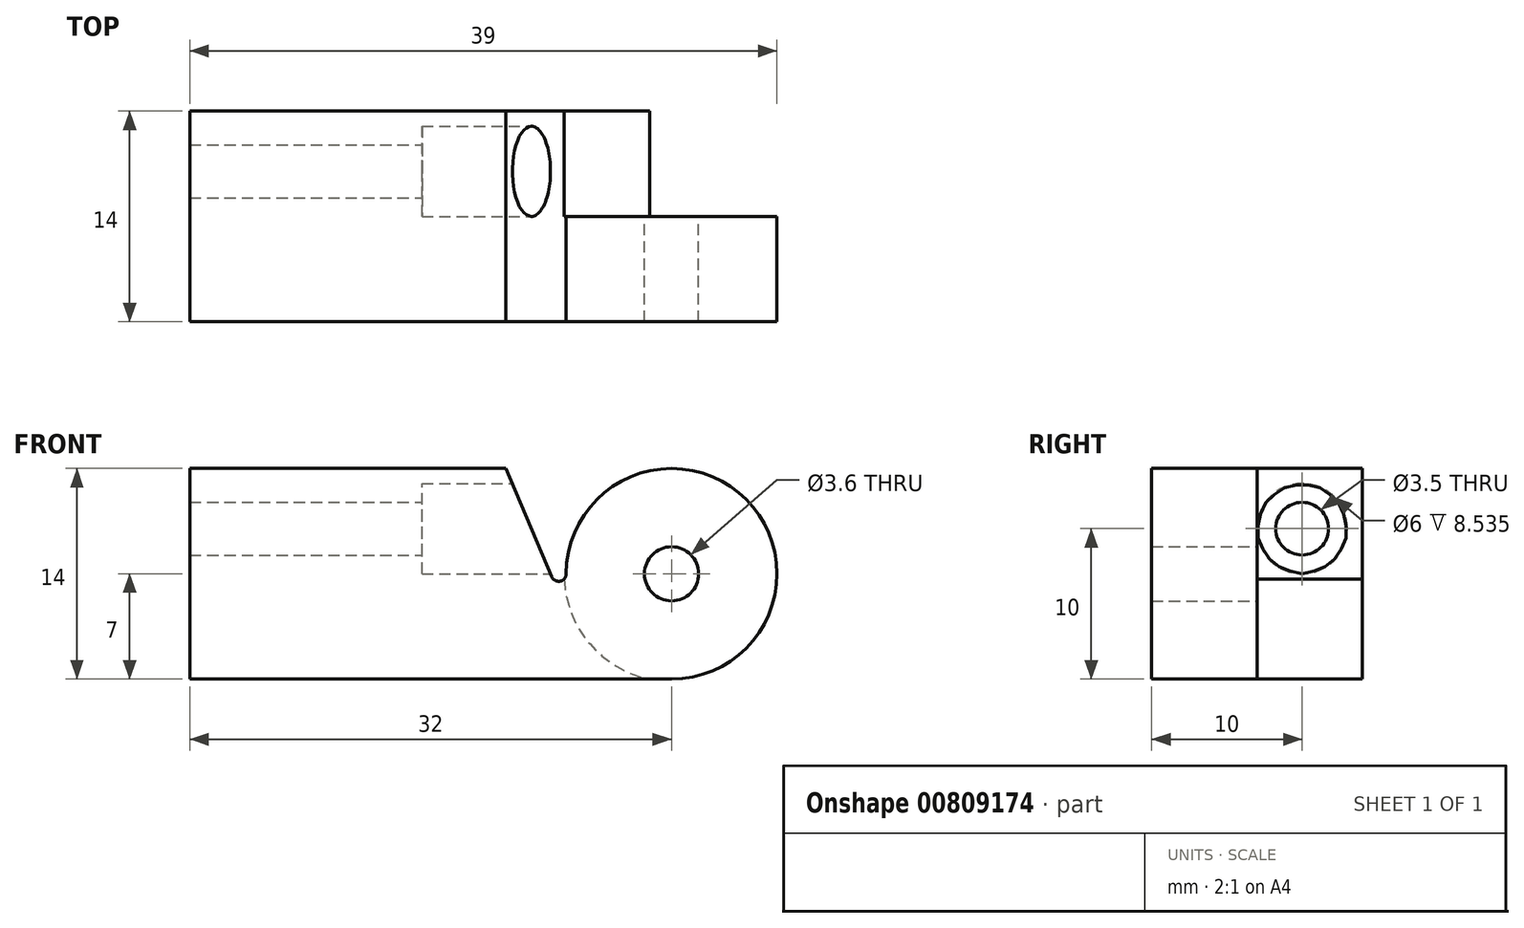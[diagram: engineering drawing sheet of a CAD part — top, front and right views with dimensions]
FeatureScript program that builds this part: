
annotation { "Feature Type Name" : "Feature", "Feature Type Description" : "" }
export const myFeature = defineFeature(function(context is Context, id is Id, definition is map)
    precondition{}
    {
        {
            var Q0;
            Q0=qCreatedBy(makeId("Front.planeOp"),FACE);
            var sketch = newSketch(context, id + "F0", { "sketchPlane" : qUnion([Q0])});
            skLineSegment(sketch, "E0", {"start": v(0, -1.46) * mm, "end": v(0, -7) * mm});
            skLineSegment(sketch, "E1", {"start": v(0, -7) * mm, "end": v(-25, -7) * mm});
            skLineSegment(sketch, "E2", {"start": v(-25, -7) * mm, "end": v(-25, 7) * mm});
            skPoint(sketch, "E3", {"position": v(-1, 0) * mm});
            skArc(sketch, "E4", {"start": v(-1, 0) * mm, "mid": v(-0.5, -0.5) * mm, "end": v(0, 0) * mm});
            skLineSegment(sketch, "E5", {"start": v(-25, 7) * mm, "end": v(-4, 7) * mm});
            skLineSegment(sketch, "E6", {"start": v(-4, 7) * mm, "end": v(-0.96, -0.2) * mm});
            skPoint(sketch, "E7", {"position": v(7, 0) * mm});
            skPoint(sketch, "E8", {"position": v(0, 0) * mm});
            skCircle(sketch, "E9", {"center": v(7, 0) * mm, "radius": 7 * mm});
            skLineSegment(sketch, "E10", {"start": v(0, -7) * mm, "end": v(7, -7) * mm});
            skArc(sketch, "E11", {"start": v(-0.14, -0.35) * mm, "mid": v(1.56, -4.65) * mm, "end": v(5.54, -7) * mm});
            skLineSegment(sketch, "E12", {"start": v(0, 0) * mm, "end": v(7, 0) * mm});
            skLineSegment(sketch, "E13", {"start": v(-4, 7) * mm, "end": v(-3.2, 5.1) * mm});
            skLineSegment(sketch, "E14", {"start": v(-1.04, 0) * mm, "end": v(-1, 0) * mm});
            skPoint(sketch, "E15.orphan", {"position": v(-3.2, 0) * mm});
            skSolve(sketch);
        }
        {
            var Q0;
            {var subQ4=sQuery(id+"F0.wireOp",EDGE,"E0");Q0=makeQuery(id+"F0.imprint","IMPRINT",FACE,{"disambiguationData":[TD([[makeQuery(id+"F0.imprint","IMPRINT",EDGE,{"derivedFrom":subQ4}),-1.0]])]});}
            var Q1;
            {var subQ0=sQuery(id+"F0.wireOp",EDGE,"E0");Q1=makeQuery(id+"F0.imprint","IMPRINT",FACE,{"disambiguationData":[TD([[makeQuery(id+"F0.imprint","IMPRINT",EDGE,{"derivedFrom":subQ0}),1.0]])]});}
            var Q2;
            {var subQ2=sQuery(id+"F0.wireOp",EDGE,"E4");var subQ5=sQuery(id+"F0.wireOp",EDGE,"E9");var subQ8=makeQuery(id+"F0.imprint","INTERSECT",VERTEX,{"derivedFrom":[subQ2,subQ5]});Q2=makeQuery(id+"F0.imprint","IMPRINT",FACE,{"disambiguationData":[TD([[makeQuery(id+"F0.imprint","IMPRINT",EDGE,{"disambiguationData":[TD([[subQ8,1.0]])],"derivedFrom":subQ2}),-1.0]])]});}
            var Q3;
            {var subQ0=sQuery(id+"F0.wireOp",EDGE,"E9");var subQ1=makeQuery(id+"F0.imprint","INTERSECT",VERTEX,{"derivedFrom":[sQuery(id+"F0.wireOp",EDGE,"E4"),subQ0]});Q3=makeQuery(id+"F0.imprint","IMPRINT",FACE,{"disambiguationData":[TD([[makeQuery(id+"F0.imprint","IMPRINT",EDGE,{"disambiguationData":[TD([[subQ1,-1.0]])],"derivedFrom":subQ0}),1.0]])]});}
            extrude(context, id + "F1", {"entities" : qUnion([Q0, Q1, Q2, Q3]), "depth" : 7 * mm, "offsetDistance" : 25 * mm});
        }
        {
            var Q0;
            Q0=sQuery(id+"F0.wireOp",VERTEX,"E7");
            var Q1;
            Q1=makeQuery(id+"F1.opExtrude","SWEPT_BODY",BODY,{"disambiguationData":[OSD([sQuery(id+"F0.wireOp",EDGE,"E1"),sQuery(id+"F0.wireOp",EDGE,"E2"),sQuery(id+"F0.wireOp",EDGE,"E4"),sQuery(id+"F0.wireOp",EDGE,"E5"),sQuery(id+"F0.wireOp",EDGE,"E6"),sQuery(id+"F0.wireOp",EDGE,"E9"),sQuery(id+"F0.wireOp",EDGE,"E10")])]});
            hole(context, id + "F2", {"style" : HoleStyle.SIMPLE, "endStyle" : HoleEndStyle.THROUGH, "oppositeDirection" : true, "holeDiameter" : 3.6 * mm, "majorDiameter" : 5 * mm, "isTappedThrough" : true, "tappedDepth" : 12 * mm, "tapClearance" : 3, "locations" : qUnion([Q0]), "scope" : qUnion([Q1])});
        }
        {
            var Q0;
            {var subQ4=sQuery(id+"F0.wireOp",EDGE,"E0");Q0=makeQuery(id+"F0.imprint","IMPRINT",FACE,{"disambiguationData":[TD([[makeQuery(id+"F0.imprint","IMPRINT",EDGE,{"derivedFrom":subQ4}),-1.0]])]});}
            var Q1;
            {var subQ0=sQuery(id+"F0.wireOp",EDGE,"E0");Q1=makeQuery(id+"F0.imprint","IMPRINT",FACE,{"disambiguationData":[TD([[makeQuery(id+"F0.imprint","IMPRINT",EDGE,{"derivedFrom":subQ0}),1.0]])]});}
            extrude(context, id + "F3", {"entities" : qUnion([Q0, Q1]), "operationType" : NewBodyOperationType.ADD, "oppositeDirection" : true, "depth" : 7 * mm, "offsetDistance" : 25 * mm});
        }
        {
            var Q0;
            Q0=qCreatedBy(makeId("Right.planeOp"),FACE);
            var sketch = newSketch(context, id + "F4", { "sketchPlane" : qUnion([Q0])});
            skLineSegment(sketch, "E16", {"start": v(0, 0) * mm, "end": v(3, 0) * mm});
            skLineSegment(sketch, "E17", {"start": v(3, 0) * mm, "end": v(3, 3) * mm});
            skPoint(sketch, "E18", {"position": v(3, 3) * mm});
            skSolve(sketch);
        }
        {
            var Q0;
            Q0=sQuery(id+"F4.wireOp",VERTEX,"E18");
            var Q1;
            Q1=makeQuery(id+"F1.opExtrude","SWEPT_BODY",BODY,{"disambiguationData":[OSD([sQuery(id+"F0.wireOp",EDGE,"E1"),sQuery(id+"F0.wireOp",EDGE,"E2"),sQuery(id+"F0.wireOp",EDGE,"E4"),sQuery(id+"F0.wireOp",EDGE,"E5"),sQuery(id+"F0.wireOp",EDGE,"E6"),sQuery(id+"F0.wireOp",EDGE,"E9"),sQuery(id+"F0.wireOp",EDGE,"E10"),sQuery(id+"F0.wireOp",EDGE,"E13")])]});
            hole(context, id + "F5", {"style" : HoleStyle.C_BORE, "endStyle" : HoleEndStyle.THROUGH, "holeDiameter" : 3.5 * mm, "cBoreDiameter" : 6 * mm, "cBoreDepth" : 6 * mm, "majorDiameter" : 5 * mm, "isTappedThrough" : true, "tappedDepth" : 12 * mm, "tapClearance" : 3, "locations" : qUnion([Q0]), "scope" : qUnion([Q1])});
        }
    });
